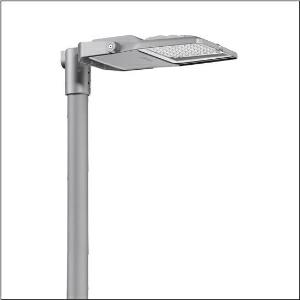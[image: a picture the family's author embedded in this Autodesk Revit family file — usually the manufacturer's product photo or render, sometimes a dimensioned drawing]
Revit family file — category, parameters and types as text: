
# Revit family: floodlight_fl_21_iq_mini___pl33t_5xa7772c2f3a_076b
name_source: partatom
category: Lighting Fixtures
units: mm (PartAtom-declared; Revit-internal decimal feet)

## family parameters
Cut with Voids When Loaded = No
Host = Face
Light Source = No
Part Type = Normal
Room Calculation Point = No
Round Connector Dimension = Use Diameter
Shared = No

## types (1)
- --- (1 x LED, 12060 lm, 87.2 W, 3000K)
    Apparent Load = 87 VA
    CIE Flux Codes = 26 75 99 100 100
    Color Rendering = 70
    Color Temperature = 3000K
    Default Elevation = 1800 mm
    Description = Floodlight FL 21 iQ mini, floodlight, primary light control with lens, of PMMA, primary optical cover: protective disc, of toughened safety glass, transparent, light distribution: PL33T, light emission: direct distribution, installation type: surface-mounted, LED, High Power LED, rated luminous flux: 12.060lm, luminous efficacy: 138lm/W, light colour: 730, colour temperature: 3000K, control: Auto-Match, Temp-Guard, Night-Set, Smart-Wire, Desk-Remote (wireless, voltage-free reading and setting of iQ features in the workshop via application-optimized NFC function/RFID function), optimised constant luminous flux control (CLO 2.0), Light-Fading, Lumen-Switch, with terminal, 6-pole, mains connection: 220..240V, AC, 50/60Hz, start of lifetime: 87W, end of service life: 92W, reduction: 40W, luminaire housing, of diecast aluminium, powder-coated, Siteco® metallic grey (DB 702S), corrosivity category C5 mid according to DIN EN ISO 12944, sealing non-destructively replaceable, please order mast flange separately, mast bracket, of steel, galvanised, powder-coated, protection rating (complete): IP66, insulation class (complete): insulation class II (safety insulation), certification: CE, ENEC, VDE, protection symbol: D, impact resistance: IK08, permissible operating ambient temperature: -40..+40°C, permissible operating ambient temperature for outdoor applications: -40..+50°C, standard: DIN EN 12944, LABS conformity tested according to VDMA 24364:2018-05, packaging unit: 1 piece

Light Distribution: PL33T
    Height = 70 mm
    Lamp = 1 x LED
    Lamp Light Flux = 12060 lm
    Lamp Power = 87.2 W
    Lamp count = 1
    Length = 485 mm
    Luminous efficacy = 138 lm/W
    Manufacturer = Siteco
    ModVariant = No
    Model = 5XA7772C2F3A
    Number of Poles = 1
    OnlyDefault = Yes
    Power Factor = 1
    Product Name = Floodlight FL 21 iQ mini | PL33T
    Product group = floodlight | pylon annexe
    ProductGroupID = 6200
    Protection Class = Protection class II
    Protection Degree = IP 66
    RLX_Detail_Level = 1
    RLX_Emergency_Light_Flux = 0 lm
    RLX_Emergency_Type = 0
    RLX_Emergency_Type_DB = No
    RlxData = <blob elided: 101173 chars, md5=c5943fff>
    Socket = socket
    Standby Power = 0 W
    System Light Flux = 12060 lm
    System Power = 87 W
    Type Comments = factory setting: luminous flux: 100 % | dim-lin: 254 | 456 mA
    Type Image = l_1007125.jpg
    URL = http://relux.com
    VarID = @adj_081975
    Voltage = 0 V
    Weight = 0.00 kg
    Width = 337 mm

## geometry (parser evidence)
native form markers: Blend x4, Sweep x12
no freeform markers — native parametric forms only
